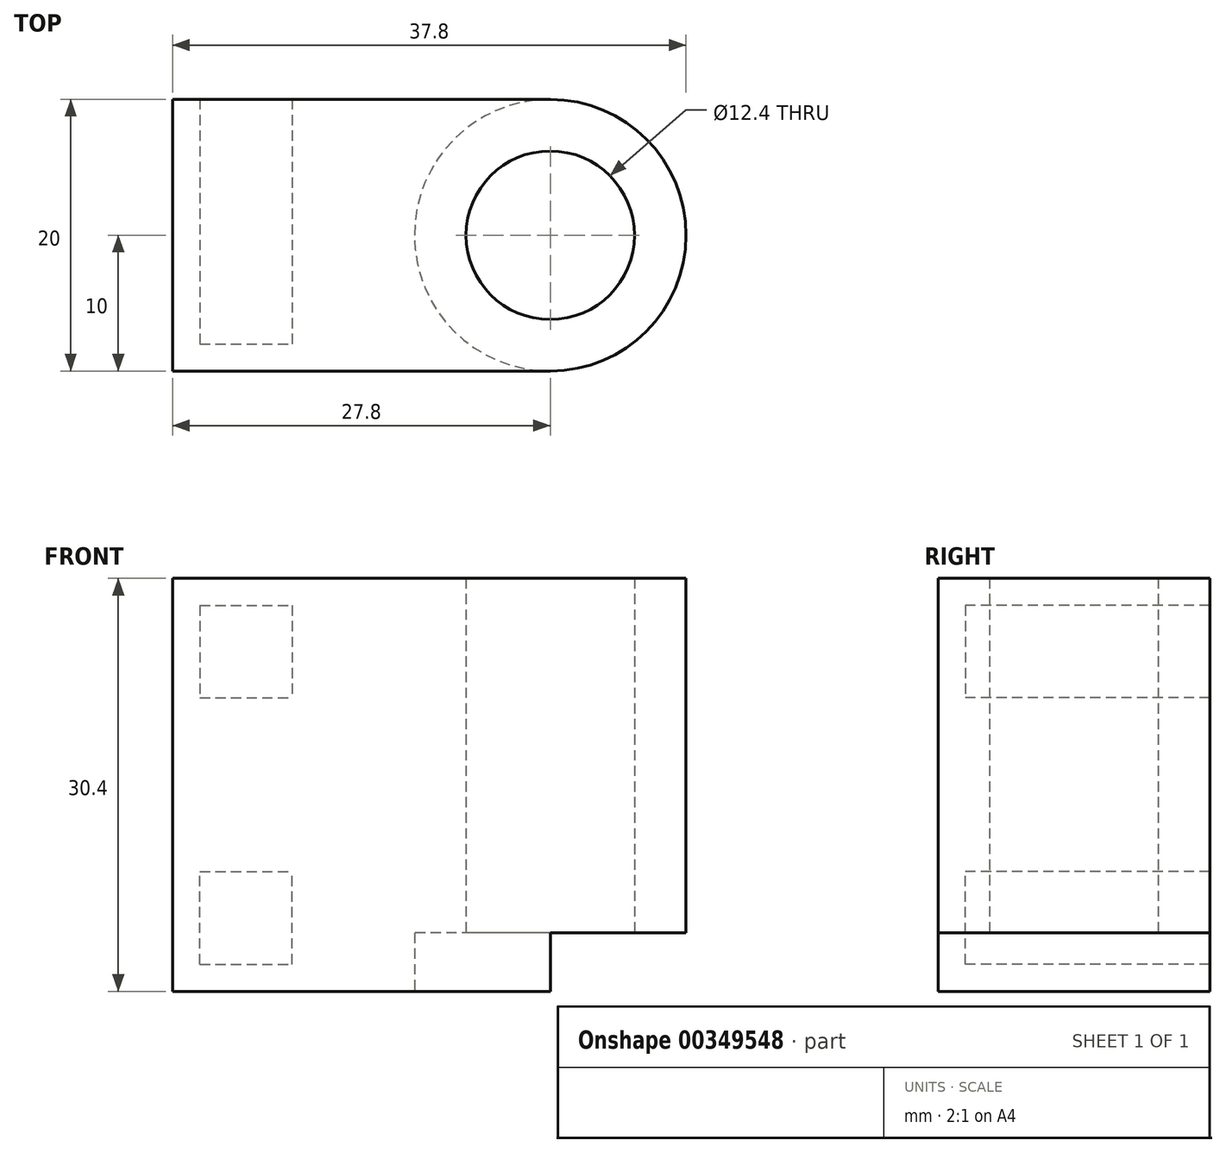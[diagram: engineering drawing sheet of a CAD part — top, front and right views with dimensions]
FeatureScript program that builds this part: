
annotation { "Feature Type Name" : "Feature", "Feature Type Description" : "" }
export const myFeature = defineFeature(function(context is Context, id is Id, definition is map)
    precondition{}
    {
        {
            var Q0;
            Q0=qCreatedBy(makeId("Top.planeOp"),FACE);
            var sketch = newSketch(context, id + "F0", { "sketchPlane" : qUnion([Q0])});
            skCircle(sketch, "E0", {"center": v(0, 0) * mm, "radius": 10 * mm});
            skLineSegment(sketch, "E1", {"start": v(0, 0) * mm, "end": v(0, 10) * mm});
            skLineSegment(sketch, "E2.bottom", {"start": v(0, 10) * mm, "end": v(-27.8, 10) * mm});
            skLineSegment(sketch, "E2.top", {"start": v(0, -10) * mm, "end": v(-27.8, -10) * mm});
            skLineSegment(sketch, "E2.left", {"start": v(0, 10) * mm, "end": v(0, -10) * mm});
            skLineSegment(sketch, "E2.right", {"start": v(-27.8, 10) * mm, "end": v(-27.8, -10) * mm});
            skCircle(sketch, "E3", {"center": v(0, 0) * mm, "radius": 5.5 * mm});
            skCircle(sketch, "E4", {"center": v(0, 0) * mm, "radius": 6.2 * mm});
            skSolve(sketch);
        }
        {
            var Q0;
            {var subQ1=sQuery(id+"F0.wireOp",EDGE,"E2.bottom");Q0=makeQuery(id+"F0.imprint","IMPRINT",FACE,{"disambiguationData":[TD([[makeQuery(id+"F0.imprint","IMPRINT",EDGE,{"derivedFrom":subQ1}),1.0]])]});}
            var Q1;
            {var subQ0=sQuery(id+"F0.wireOp",EDGE,"E2.left");var subQ1=sQuery(id+"F0.wireOp",EDGE,"jRdqZ9CW-k9WA-U4WL-7JIf-AR9hrelphjrp");var subQ2=makeQuery(id+"F0.imprint","INTERSECT",VERTEX,{"disambiguationData":[OD(0.0)],"derivedFrom":[subQ1,subQ0]});Q1=makeQuery(id+"F0.imprint","IMPRINT",FACE,{"disambiguationData":[TD([[makeQuery(id+"F0.imprint","IMPRINT",EDGE,{"disambiguationData":[TD([[subQ2,-1.0]])],"derivedFrom":subQ1}),-1.0]])]});}
            var Q2;
            {var subQ0=sQuery(id+"F0.wireOp",EDGE,"E2.left");var subQ1=sQuery(id+"F0.wireOp",EDGE,"jRdqZ9CW-k9WA-U4WL-7JIf-AR9hrelphjrp");var subQ2=makeQuery(id+"F0.imprint","INTERSECT",VERTEX,{"disambiguationData":[OD(0.0)],"derivedFrom":[subQ1,subQ0]});Q2=makeQuery(id+"F0.imprint","IMPRINT",FACE,{"disambiguationData":[TD([[makeQuery(id+"F0.imprint","IMPRINT",EDGE,{"disambiguationData":[TD([[subQ2,1.0]])],"derivedFrom":subQ1}),-1.0]])]});}
            var Q3;
            {var subQ0=sQuery(id+"F0.wireOp",EDGE,"E2.left");var subQ4=sQuery(id+"F0.wireOp",EDGE,"E4");var subQ5=makeQuery(id+"F0.imprint","INTERSECT",VERTEX,{"disambiguationData":[OD(0.0)],"derivedFrom":[subQ0,subQ4]});Q3=makeQuery(id+"F0.imprint","IMPRINT",FACE,{"disambiguationData":[TD([[makeQuery(id+"F0.imprint","IMPRINT",EDGE,{"disambiguationData":[TD([[subQ5,1.0]])],"derivedFrom":subQ4}),-1.0]])]});}
            var Q4;
            {var subQ0=sQuery(id+"F0.wireOp",EDGE,"E2.left");var subQ4=sQuery(id+"F0.wireOp",EDGE,"E4");var subQ5=makeQuery(id+"F0.imprint","INTERSECT",VERTEX,{"disambiguationData":[OD(0.0)],"derivedFrom":[subQ0,subQ4]});Q4=makeQuery(id+"F0.imprint","IMPRINT",FACE,{"disambiguationData":[TD([[makeQuery(id+"F0.imprint","IMPRINT",EDGE,{"disambiguationData":[TD([[subQ5,-1.0]])],"derivedFrom":subQ4}),-1.0]])]});}
            var Q5;
            {var subQ0=sQuery(id+"F0.wireOp",EDGE,"E4");var subQ1=sQuery(id+"F0.wireOp",EDGE,"E2.left");var subQ2=makeQuery(id+"F0.imprint","INTERSECT",VERTEX,{"disambiguationData":[OD(0.0)],"derivedFrom":[subQ1,subQ0]});Q5=makeQuery(id+"F0.imprint","IMPRINT",FACE,{"disambiguationData":[TD([[makeQuery(id+"F0.imprint","IMPRINT",EDGE,{"disambiguationData":[TD([[subQ2,-1.0]])],"derivedFrom":subQ1}),1.0]])]});}
            var Q6;
            {var subQ0=sQuery(id+"F0.wireOp",EDGE,"E4");var subQ1=sQuery(id+"F0.wireOp",EDGE,"E2.left");var subQ2=makeQuery(id+"F0.imprint","INTERSECT",VERTEX,{"disambiguationData":[OD(0.0)],"derivedFrom":[subQ1,subQ0]});Q6=makeQuery(id+"F0.imprint","IMPRINT",FACE,{"disambiguationData":[TD([[makeQuery(id+"F0.imprint","IMPRINT",EDGE,{"disambiguationData":[TD([[subQ2,-1.0]])],"derivedFrom":subQ1}),-1.0]])]});}
            extrude(context, id + "F1", {"entities" : qUnion([Q0, Q1, Q2, Q3, Q4, Q5, Q6]), "depth" : 30.4 * mm});
        }
        {
            var Q0;
            Q0=makeQuery(id+"F1.opExtrude","SWEPT_FACE",FACE,{"disambiguationData":[OSD([sQuery(id+"F0.wireOp",EDGE,"E2.top")])]});
            var sketch = newSketch(context, id + "F2", { "sketchPlane" : qUnion([Q0])});
            skLineSegment(sketch, "E5.bottom", {"start": v(-27.8, 30.4) * mm, "end": v(-25.8, 30.4) * mm});
            skLineSegment(sketch, "E5.top", {"start": v(-27.8, 28.4) * mm, "end": v(-25.8, 28.4) * mm});
            skLineSegment(sketch, "E5.left", {"start": v(-27.8, 30.4) * mm, "end": v(-27.8, 28.4) * mm});
            skLineSegment(sketch, "E5.right", {"start": v(-25.8, 30.4) * mm, "end": v(-25.8, 28.4) * mm});
            skLineSegment(sketch, "E6.bottom", {"start": v(-25.8, 28.4) * mm, "end": v(-19, 28.4) * mm});
            skLineSegment(sketch, "E6.top", {"start": v(-25.8, 21.6) * mm, "end": v(-19, 21.6) * mm});
            skLineSegment(sketch, "E6.left", {"start": v(-25.8, 28.4) * mm, "end": v(-25.8, 21.6) * mm});
            skLineSegment(sketch, "E6.right", {"start": v(-19, 28.4) * mm, "end": v(-19, 21.6) * mm});
            skPoint(sketch, "E7", {"position": v(-27.8, 15.2) * mm});
            skLineSegment(sketch, "E8", {"start": v(-27.8, 15.2) * mm, "end": v(0, 15.2) * mm});
            skLineSegment(sketch, "E9.MirrorCS", {"start": v(-25.8, 8.8) * mm, "end": v(-19, 8.8) * mm});
            skLineSegment(sketch, "E10.MirrorCS", {"start": v(-19, 2) * mm, "end": v(-19, 8.8) * mm});
            skLineSegment(sketch, "E11.MirrorCS", {"start": v(-25.8, 2) * mm, "end": v(-19, 2) * mm});
            skLineSegment(sketch, "E12.MirrorCS", {"start": v(-25.8, 2) * mm, "end": v(-25.8, 8.8) * mm});
            skSolve(sketch);
        }
        {
            var Q0;
            Q0=makeQuery(id+"F2.imprint","IMPRINT",FACE,{"disambiguationData":[TD([[makeQuery(id+"F2.imprint","IMPRINT",EDGE,{"derivedFrom":sQuery(id+"F2.wireOp",EDGE,"E6.bottom")}),-1.0]])]});
            var Q1;
            Q1=makeQuery(id+"F2.imprint","IMPRINT",FACE,{"disambiguationData":[TD([[makeQuery(id+"F2.imprint","IMPRINT",EDGE,{"derivedFrom":sQuery(id+"F2.wireOp",EDGE,"E9.MirrorCS")}),-1.0]])]});
            extrude(context, id + "F3", {"entities" : qUnion([Q0, Q1]), "operationType" : NewBodyOperationType.REMOVE, "oppositeDirection" : true, "depth" : 50 * mm});
        }
        {
            var Q0;
            Q0=makeQuery(id+"F1.opExtrude","CAP_FACE",FACE,{"disambiguationData":[OSD([sQuery(id+"F0.wireOp",EDGE,"E0"),sQuery(id+"F0.wireOp",EDGE,"E2.bottom"),sQuery(id+"F0.wireOp",EDGE,"E2.top"),sQuery(id+"F0.wireOp",EDGE,"E2.right"),sQuery(id+"F0.wireOp",EDGE,"E3")])],"isStart":false});
            var sketch = newSketch(context, id + "F4", { "sketchPlane" : qUnion([Q0])});
            skCircle(sketch, "E13", {"center": v(0, 0) * mm, "radius": 6.2 * mm});
            skSolve(sketch);
        }
        {
            var Q0;
            Q0=makeQuery(id+"F4.imprint","IMPRINT",FACE,{"disambiguationData":[TD([[makeQuery(id+"F4.imprint","IMPRINT",EDGE,{"derivedFrom":sQuery(id+"F4.wireOp",EDGE,"E13")}),1.0]])]});
            extrude(context, id + "F5", {"entities" : qUnion([Q0]), "operationType" : NewBodyOperationType.REMOVE, "oppositeDirection" : true, "depth" : 4.3 * mm});
        }
        {
            var Q0;
            {var subQ0=sQuery(id+"F0.wireOp",EDGE,"E4");var subQ1=sQuery(id+"F0.wireOp",EDGE,"E2.left");var subQ2=makeQuery(id+"F0.imprint","INTERSECT",VERTEX,{"disambiguationData":[OD(0.0)],"derivedFrom":[subQ1,subQ0]});Q0=makeQuery(id+"F0.imprint","IMPRINT",FACE,{"disambiguationData":[TD([[makeQuery(id+"F0.imprint","IMPRINT",EDGE,{"disambiguationData":[TD([[subQ2,-1.0]])],"derivedFrom":subQ1}),-1.0]])]});}
            var Q1;
            {var subQ0=sQuery(id+"F0.wireOp",EDGE,"E4");var subQ1=sQuery(id+"F0.wireOp",EDGE,"E2.left");var subQ2=makeQuery(id+"F0.imprint","INTERSECT",VERTEX,{"disambiguationData":[OD(0.0)],"derivedFrom":[subQ1,subQ0]});Q1=makeQuery(id+"F0.imprint","IMPRINT",FACE,{"disambiguationData":[TD([[makeQuery(id+"F0.imprint","IMPRINT",EDGE,{"disambiguationData":[TD([[subQ2,-1.0]])],"derivedFrom":subQ1}),1.0]])]});}
            extrude(context, id + "F6", {"entities" : qUnion([Q0, Q1]), "operationType" : NewBodyOperationType.REMOVE, "depth" : 4.3 * mm});
        }
        {
            var Q0;
            Q0=makeQuery(id+"F2.imprint","IMPRINT",FACE,{"disambiguationData":[TD([[makeQuery(id+"F2.imprint","IMPRINT",EDGE,{"derivedFrom":sQuery(id+"F2.wireOp",EDGE,"E6.bottom")}),-1.0]])]});
            var Q1;
            Q1=makeQuery(id+"F2.imprint","IMPRINT",FACE,{"disambiguationData":[TD([[makeQuery(id+"F2.imprint","IMPRINT",EDGE,{"derivedFrom":sQuery(id+"F2.wireOp",EDGE,"E9.MirrorCS")}),-1.0]])]});
            extrude(context, id + "F7", {"entities" : qUnion([Q0, Q1]), "operationType" : NewBodyOperationType.ADD, "oppositeDirection" : true, "depth" : 2 * mm});
        }
    });
